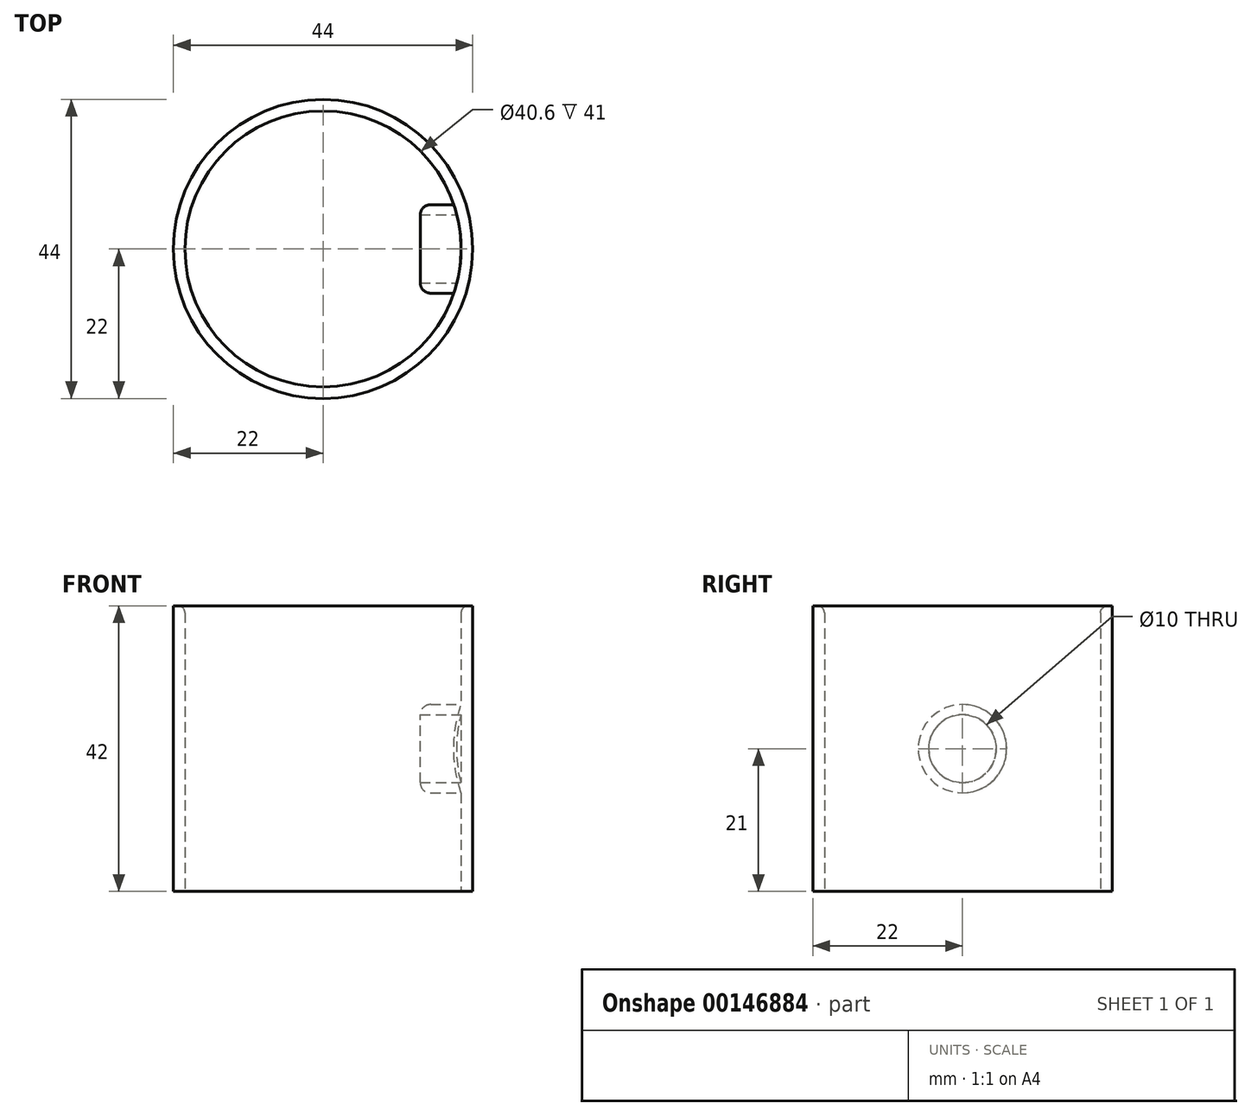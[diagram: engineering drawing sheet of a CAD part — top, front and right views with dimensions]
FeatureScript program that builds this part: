
annotation { "Feature Type Name" : "Feature", "Feature Type Description" : "" }
export const myFeature = defineFeature(function(context is Context, id is Id, definition is map)
    precondition{}
    {
        {
            var Q0;
            Q0=qCreatedBy(makeId("Top.planeOp"),FACE);
            var sketch = newSketch(context, id + "F0", { "sketchPlane" : qUnion([Q0])});
            skCircle(sketch, "E0", {"center": v(0, 0) * mm, "radius": 22 * mm});
            skCircle(sketch, "E1", {"center": v(0, 0) * mm, "radius": 20.3 * mm});
            skPoint(sketch, "E2", {"position": v(0, -20.3) * mm});
            skPoint(sketch, "E3", {"position": v(0, 20.3) * mm});
            skLineSegment(sketch, "E4", {"start": v(0, -22) * mm, "end": v(0, 22) * mm});
            skPoint(sketch, "E5", {"position": v(20.3, 0) * mm});
            skPoint(sketch, "E6", {"position": v(-20.3, 0) * mm});
            skSolve(sketch);
        }
        {
            var Q0;
            {var subQ0=sQuery(id+"F0.wireOp",EDGE,"E4");var subQ1=sQuery(id+"F0.wireOp",EDGE,"E0");var subQ2=makeQuery(id+"F0.imprint","INTERSECT",VERTEX,{"disambiguationData":[OD(0.0)],"derivedFrom":[subQ1,subQ0]});Q0=makeQuery(id+"F0.imprint","IMPRINT",FACE,{"disambiguationData":[TD([[makeQuery(id+"F0.imprint","IMPRINT",EDGE,{"disambiguationData":[TD([[subQ2,-1.0]])],"derivedFrom":subQ1}),1.0]])]});}
            extrude(context, id + "F1", {"entities" : qUnion([Q0]), "depth" : 42 * mm});
        }
        {
            var Q0;
            Q0=qCreatedBy(makeId("Right.planeOp"),FACE);
            var Q1;
            Q1=sQuery(id+"F0.wireOp",VERTEX,"E5");
            cPlane(context, id + "F2", {"entities" : qUnion([Q0, Q1]), "cplaneType" : CPlaneType.PLANE_POINT, "offset" : 25 * mm, "width" : 150 * mm, "height" : 150 * mm});
        }
        {
            var Q0;
            Q0=qCreatedBy(id+"F2.planeOp",FACE);
            var sketch = newSketch(context, id + "F3", { "sketchPlane" : qUnion([Q0])});
            skPoint(sketch, "E7", {"position": v(0, 21) * mm});
            skCircle(sketch, "E8", {"center": v(0, 21) * mm, "radius": 5 * mm});
            skCircle(sketch, "E9", {"center": v(0, 21) * mm, "radius": 6.5 * mm});
            skSolve(sketch);
        }
        {
            var Q0;
            Q0=qSketchRegion(id+"F3",true);
            extrude(context, id + "F4", {"entities" : qUnion([Q0]), "operationType" : NewBodyOperationType.ADD, "oppositeDirection" : true, "depth" : 6 * mm});
        }
        {
            var Q0;
            Q0=makeQuery(id+"F3.imprint","IMPRINT",FACE,{"disambiguationData":[TD([[makeQuery(id+"F3.imprint","IMPRINT",EDGE,{"derivedFrom":sQuery(id+"F3.wireOp",EDGE,"E8")}),1.0]])]});
            extrude(context, id + "F5", {"entities" : qUnion([Q0]), "operationType" : NewBodyOperationType.REMOVE, "depth" : 1 * mm});
        }
        {
            var Q0;
            Q0=makeQuery(id+"F1.opExtrude","SWEPT_BODY",BODY,{"disambiguationData":[OSD([sQuery(id+"F0.wireOp",EDGE,"E0"),sQuery(id+"F0.wireOp",EDGE,"E1"),sQuery(id+"F0.wireOp",EDGE,"E4")])]});
            var Q1;
            Q1=qCreatedBy(makeId("Right.planeOp"),FACE);
            mirror(context, id + "F6", {"operationType" : NewBodyOperationType.ADD, "entities" : qUnion([Q0]), "mirrorPlane" : qUnion([Q1])});
        }
        {
            var Q0;
            {var subQ0=makeQuery(id+"F1.opExtrude","CAP_EDGE",EDGE,{"disambiguationData":[OSD([sQuery(id+"F0.wireOp",EDGE,"E1")])],"isStart":false});Q0=makeQuery(id+"F6.boolean.opBoolean","MERGE",EDGE,{"derivedFrom":[subQ0,makeQuery(id+"F6.opPattern","COPY",EDGE,{"derivedFrom":subQ0,"instanceName":"1"})]});}
            fillet(context, id + "F7", {"entities" : qUnion([Q0]), "radius" : 1 * mm, "tangentPropagation" : true, "allowEdgeOverflow" : false});
        }
        {
            var Q0;
            Q0=makeQuery(id+"F4.opExtrude","CAP_EDGE",EDGE,{"disambiguationData":[OSD([sQuery(id+"F3.wireOp",EDGE,"E9")])],"isStart":false});
            var Q1;
            Q1=makeQuery(id+"F6.opPattern","COPY",EDGE,{"derivedFrom":makeQuery(id+"F4.opExtrude","CAP_EDGE",EDGE,{"disambiguationData":[OSD([sQuery(id+"F3.wireOp",EDGE,"E9")])],"isStart":false}),"instanceName":"1"});
            fillet(context, id + "F8", {"entities" : qUnion([Q0, Q1]), "radius" : 1.5 * mm, "tangentPropagation" : true, "allowEdgeOverflow" : false});
        }
    });
